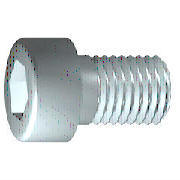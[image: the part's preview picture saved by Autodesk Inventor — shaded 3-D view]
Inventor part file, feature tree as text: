
AUTODESK INVENTOR PART (.ipt)
format: ipt  version: 2024 (Build 280153000, 153)  size: 192,000 bytes
history: native  units: mm (DEFAULTED — no unit token found)
features: fillet x2, sketch x2, extrude x1, thread x1, chamfer x1, plane x1
ambient origin geometry x7: Origin, YZ Plane, XY Plane, X Axis, Y Axis, Z Axis, Center Point
bodies: Solid1 (feature_tree), Body (feature_tree)
feature tree (8):
  extrude  "Slot"  Depth=3.0mm
  fillet  "Fillet1"  Radius=3.0mm
  thread  "Thread"  [1 undecoded]
  chamfer  "Chamfer1"  Distance=3.0mm
  plane  "Work Plane1"
  fillet  "Fillet2"  Radius=3.0mm
  sketch  "Sketch1"  dims[d1=8.75mm d2=0.306825mm d3=3.0mm d4=1.3mm]
  sketch  "Sketch2"  dims[d5=60.0deg d6=3.0mm d7=3.0mm d8=2.886751mm d9=5.5mm d10=90.0deg d11=10.0mm d12=0.0mm d13=8.75mm d14=0.0mm d15=0.306725mm d16=0.306725mm d17=0.3mm d19=0.0mm d26=10.0mm d27=45.0deg d28=0.0mm d29=0.0mm d30=0.1mm]
note: 1 required parameter value undecoded (feature->parameter linkage not recoverable at this tier; creation-order binding heuristic only, values carry confidence <= 0.55)
